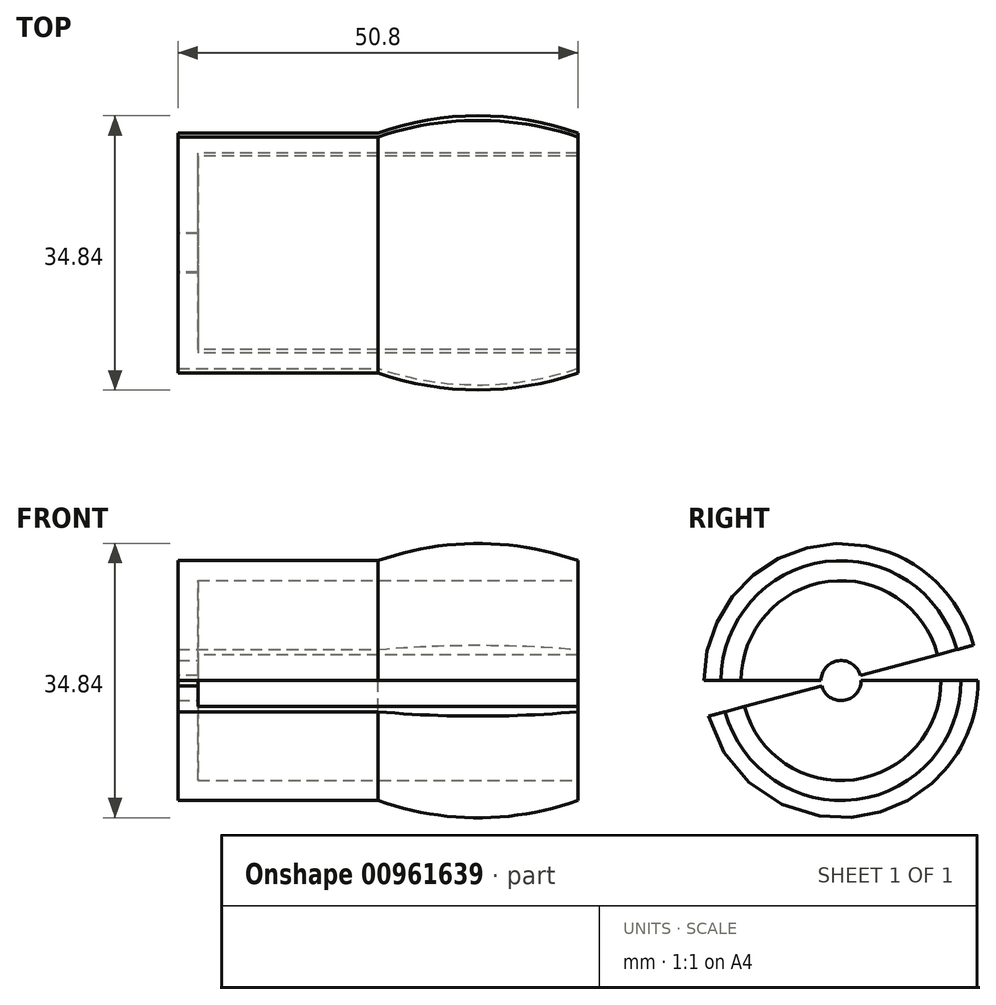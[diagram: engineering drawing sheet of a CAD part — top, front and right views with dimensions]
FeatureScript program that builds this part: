
annotation { "Feature Type Name" : "Feature", "Feature Type Description" : "" }
export const myFeature = defineFeature(function(context is Context, id is Id, definition is map)
    precondition{}
    {
        {
            var Q0;
            Q0=qCreatedBy(makeId("Top.planeOp"),FACE);
            var sketch = newSketch(context, id + "F0", { "sketchPlane" : qUnion([Q0])});
            skLineSegment(sketch, "E0", {"start": v(33.22, 0) * mm, "end": v(-33.22, 0) * mm});
            skLineSegment(sketch, "E1", {"start": v(-33.22, -2.54) * mm, "end": v(-35.76, -2.54) * mm});
            skLineSegment(sketch, "E2", {"start": v(-33.22, -2.54) * mm, "end": v(-33.22, -12.7) * mm});
            skLineSegment(sketch, "E3", {"start": v(-35.76, -2.54) * mm, "end": v(-35.76, -15.24) * mm});
            skLineSegment(sketch, "E4", {"start": v(-35.76, -15.24) * mm, "end": v(-10.36, -15.24) * mm});
            skLineSegment(sketch, "E5", {"start": v(15.04, -15.24) * mm, "end": v(15.04, -12.7) * mm});
            skLineSegment(sketch, "E6", {"start": v(15.04, -12.7) * mm, "end": v(-33.22, -12.7) * mm});
            skArc(sketch, "E7", {"start": v(-10.36, -15.24) * mm, "mid": v(2.34, -17.42) * mm, "end": v(15.04, -15.24) * mm});
            skLineSegment(sketch, "E8.MirrorCS", {"start": v(-33.22, 2.54) * mm, "end": v(-35.76, 2.54) * mm});
            skLineSegment(sketch, "E9.MirrorCS", {"start": v(-35.76, 15.24) * mm, "end": v(-10.36, 15.24) * mm});
            skArc(sketch, "E10.MirrorCS", {"start": v(-10.36, 15.24) * mm, "mid": v(2.34, 17.42) * mm, "end": v(15.04, 15.24) * mm});
            skLineSegment(sketch, "E11.MirrorCS", {"start": v(15.04, 15.24) * mm, "end": v(15.04, 12.7) * mm});
            skLineSegment(sketch, "E12.MirrorCS", {"start": v(-35.76, 2.54) * mm, "end": v(-35.76, 15.24) * mm});
            skLineSegment(sketch, "E13.MirrorCS", {"start": v(-33.22, 2.54) * mm, "end": v(-33.22, 12.7) * mm});
            skLineSegment(sketch, "E14.MirrorCS", {"start": v(15.04, 12.7) * mm, "end": v(-33.22, 12.7) * mm});
            skSolve(sketch);
        }
        {
            var Q0;
            Q0=makeQuery(id+"F0.imprint","IMPRINT",FACE,{"disambiguationData":[TD([[makeQuery(id+"F0.imprint","IMPRINT",EDGE,{"derivedFrom":sQuery(id+"F0.wireOp",EDGE,"E8.MirrorCS")}),-1.0]])]});
            var Q1;
            Q1=sQuery(id+"F0.wireOp",EDGE,"E0");
            revolve(context, id + "F1", {"surfaceOperationType" : NewSurfaceOperationType.NEW, "entities" : qUnion([Q0]), "axis" : qUnion([Q1]), "revolveType" : RevolveType.ONE_DIRECTION, "angle" : 165 * degree});
        }
        {
            var Q0;
            Q0=makeQuery(id+"F0.imprint","IMPRINT",FACE,{"disambiguationData":[TD([[makeQuery(id+"F0.imprint","IMPRINT",EDGE,{"derivedFrom":sQuery(id+"F0.wireOp",EDGE,"E1")}),1.0]])]});
            var Q1;
            Q1=sQuery(id+"F0.wireOp",EDGE,"E0");
            revolve(context, id + "F2", {"surfaceOperationType" : NewSurfaceOperationType.NEW, "entities" : qUnion([Q0]), "axis" : qUnion([Q1]), "revolveType" : RevolveType.ONE_DIRECTION, "angle" : 165 * degree});
        }
    });
